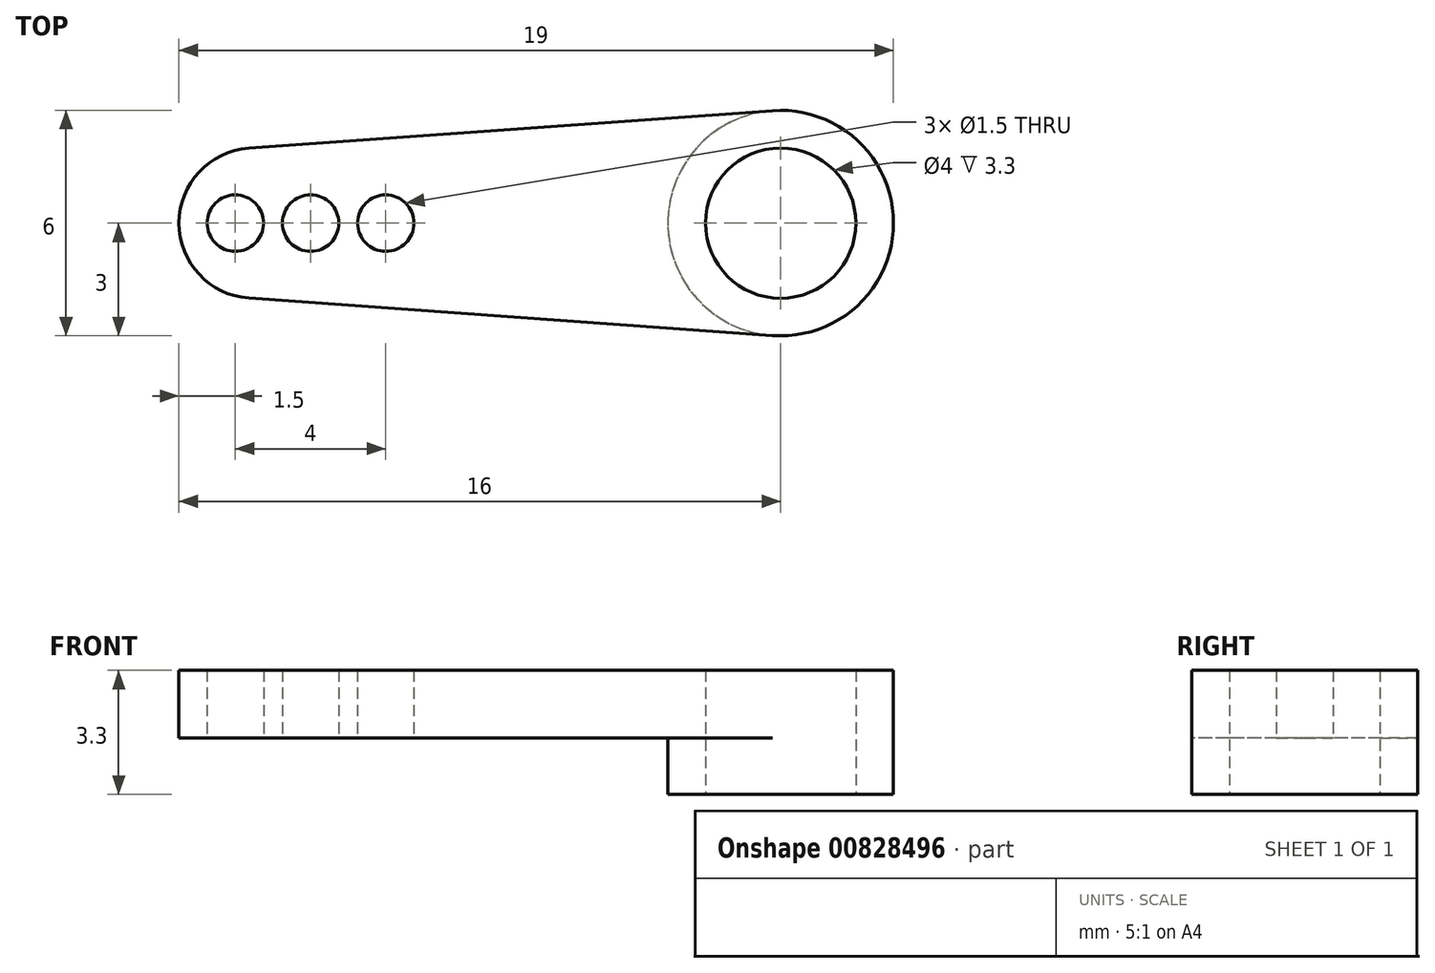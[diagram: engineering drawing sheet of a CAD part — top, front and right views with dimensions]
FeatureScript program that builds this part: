
annotation { "Feature Type Name" : "Feature", "Feature Type Description" : "" }
export const myFeature = defineFeature(function(context is Context, id is Id, definition is map)
    precondition{}
    {
        {
            var Q0;
            Q0=qCreatedBy(makeId("Top.planeOp"),FACE);
            var sketch = newSketch(context, id + "F0", { "sketchPlane" : qUnion([Q0])});
            skArc(sketch, "E0", {"start": v(-0.21, -3) * mm, "mid": v(3, 0) * mm, "end": v(-0.21, 3) * mm});
            skLineSegment(sketch, "E1", {"start": v(3, 0) * mm, "end": v(-16, 0) * mm, "construction": true});
            skPoint(sketch, "E2", {"position": v(-16, 0) * mm});
            skArc(sketch, "E3", {"start": v(-14.14, 2) * mm, "mid": v(-16, 0) * mm, "end": v(-14.14, -2) * mm});
            skLineSegment(sketch, "E4", {"start": v(-0.21, 3) * mm, "end": v(-0.21, -3) * mm, "construction": true});
            skLineSegment(sketch, "E5", {"start": v(-14.14, 2) * mm, "end": v(-14.14, -2) * mm, "construction": true});
            skLineSegment(sketch, "E6", {"start": v(-14.14, 2) * mm, "end": v(-0.21, 3) * mm});
            skLineSegment(sketch, "E7", {"start": v(-14.14, -2) * mm, "end": v(-0.21, -3) * mm});
            skCircle(sketch, "E8", {"center": v(0, 0) * mm, "radius": 2 * mm});
            skCircle(sketch, "E9", {"center": v(-14.5, 0) * mm, "radius": 0.75 * mm});
            skCircle(sketch, "E10", {"center": v(-12.5, 0) * mm, "radius": 0.75 * mm});
            skCircle(sketch, "E11", {"center": v(-10.5, 0) * mm, "radius": 0.75 * mm});
            skSolve(sketch);
        }
        {
            var Q0;
            Q0=makeQuery(id+"F0.imprint","IMPRINT",FACE,{"disambiguationData":[TD([[makeQuery(id+"F0.imprint","IMPRINT",EDGE,{"derivedFrom":sQuery(id+"F0.wireOp",EDGE,"E0")}),1.0]])]});
            extrude(context, id + "F1", {"entities" : qUnion([Q0]), "depth" : 1.8 * mm, "offsetDistance" : 25 * mm});
        }
        {
            var Q0;
            Q0=makeQuery(id+"F1.opExtrude","CAP_FACE",FACE,{"disambiguationData":[OSD([sQuery(id+"F0.wireOp",EDGE,"E0"),sQuery(id+"F0.wireOp",EDGE,"E3"),sQuery(id+"F0.wireOp",EDGE,"E6"),sQuery(id+"F0.wireOp",EDGE,"E7"),sQuery(id+"F0.wireOp",EDGE,"E8"),sQuery(id+"F0.wireOp",EDGE,"E9"),sQuery(id+"F0.wireOp",EDGE,"E10"),sQuery(id+"F0.wireOp",EDGE,"E11")])],"isStart":true});
            var sketch = newSketch(context, id + "F2", { "sketchPlane" : qUnion([Q0])});
            skPoint(sketch, "E12.0", {"position": v(0, 0) * mm});
            skArc(sketch, "E12.1", {"start": v(-0.21, 3) * mm, "mid": v(3, 0) * mm, "end": v(-0.21, -3) * mm});
            skArc(sketch, "E13", {"start": v(-0.21, 3) * mm, "mid": v(-3, 0) * mm, "end": v(-0.21, -3) * mm});
            skCircle(sketch, "E14.0", {"center": v(0, 0) * mm, "radius": 2 * mm});
            skSolve(sketch);
        }
        {
            var Q0;
            Q0=makeQuery(id+"F2.imprint","IMPRINT",FACE,{"disambiguationData":[TD([[makeQuery(id+"F2.imprint","IMPRINT",EDGE,{"derivedFrom":sQuery(id+"F2.wireOp",EDGE,"E12.1")}),-1.0]])]});
            extrude(context, id + "F3", {"entities" : qUnion([Q0]), "operationType" : NewBodyOperationType.ADD, "depth" : 1.5 * mm, "offsetDistance" : 25 * mm});
        }
    });
